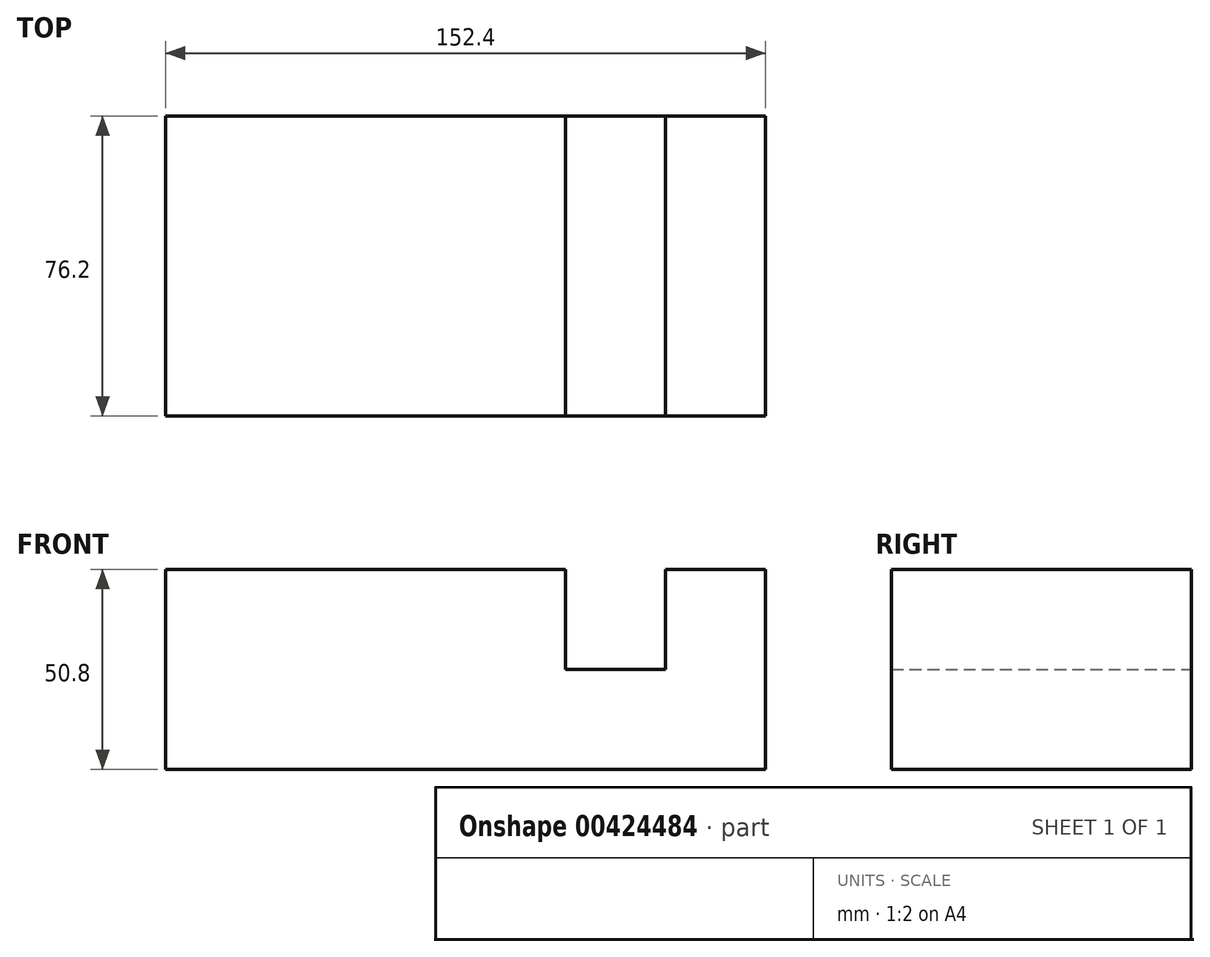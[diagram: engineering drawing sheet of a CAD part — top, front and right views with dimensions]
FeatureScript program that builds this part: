
annotation { "Feature Type Name" : "Feature", "Feature Type Description" : "" }
export const myFeature = defineFeature(function(context is Context, id is Id, definition is map)
    precondition{}
    {
        {
            var Q0;
            Q0=qCreatedBy(makeId("Front.planeOp"),FACE);
            var sketch = newSketch(context, id + "F0", { "sketchPlane" : qUnion([Q0])});
            skLineSegment(sketch, "E0", {"start": v(0, 0) * mm, "end": v(152.4, 0) * mm});
            skLineSegment(sketch, "E1", {"start": v(0, 0) * mm, "end": v(0, 50.8) * mm});
            skLineSegment(sketch, "E2", {"start": v(152.4, 0) * mm, "end": v(152.4, 50.8) * mm});
            skLineSegment(sketch, "E3", {"start": v(152.4, 50.8) * mm, "end": v(127, 50.8) * mm});
            skLineSegment(sketch, "E4", {"start": v(127, 50.8) * mm, "end": v(127, 25.4) * mm});
            skLineSegment(sketch, "E5", {"start": v(127, 25.4) * mm, "end": v(101.6, 25.4) * mm});
            skLineSegment(sketch, "E6", {"start": v(101.6, 25.4) * mm, "end": v(101.6, 50.8) * mm});
            skLineSegment(sketch, "E7", {"start": v(101.6, 50.8) * mm, "end": v(0, 50.8) * mm});
            skSolve(sketch);
        }
        {
            var Q0;
            Q0=makeQuery(id+"F0.imprint","IMPRINT",FACE,{"disambiguationData":[TD([[makeQuery(id+"F0.imprint","IMPRINT",EDGE,{"derivedFrom":sQuery(id+"F0.wireOp",EDGE,"E0")}),1.0]])]});
            extrude(context, id + "F1", {"entities" : qUnion([Q0]), "depth" : 76.2 * mm});
        }
    });
